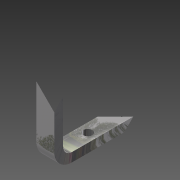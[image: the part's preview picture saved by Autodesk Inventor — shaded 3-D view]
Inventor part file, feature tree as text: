
AUTODESK INVENTOR PART (.ipt)
format: ipt  version: 2015 (Build 190159000, 159)  size: 120,832 bytes
history: native  units: mm
features: other x7, sketch x3, hole x1, fillet x1
ambient origin geometry x8: Origin, YZ Plane, XZ Plane, XY Plane, X Axis, Y Axis, Z Axis, Center Point
bodies: Body1 (feature_tree)
feature tree (12):
  other  "Bryła1"
  other  "Powierzchnia1"
  other  "Kołnierz1"
  hole  "Otwór4"  [1 undecoded]
  fillet  "Zaokrąglenie2"  Radius=10.0mm
  sketch  "Szkic1"
  other  "Płyta1"
  sketch  "Szkic2"
  sketch  "Szkic3"
  other  "Płyta2"
  other  "Gięcie1"
  other  "Narożnik1"
note: 1 required parameter value undecoded (feature->parameter linkage not recoverable at this tier; creation-order binding heuristic only, values carry confidence <= 0.55)
